# Revit family: Electrical-Box_FSR_RFL45-D2G
name_source: partatom
category: Electrical Fixtures
units: mm (PartAtom-declared; Revit-internal decimal feet)

## family parameters
Cut with Voids When Loaded = No
Host = Face
Maintain Annotation Orientation = No
Part Type = Normal
Room Calculation Point = No
Round Connector Dimension = Use Diameter
Shared = No

## types (3) — shared parameters
Apparent Load = 0 VA
Assembly Code = D5020100
Body Material = Material and Finish as Specified in 26 27 26
Building Codes = ftp://doclib.fsrinc.com/
Connections = (2) - 1/2"; (6) - 1/2 - 3/4; (2) 1" - 1 1/4" Knockouts; (3) 1x2" Oval Knockouts
Construction Details = ftp://doclib.fsrinc.com/
Default Elevation = 48 "
Green Building-LEED = http://www.arcat.com
Installation-Fabrication = ftp://doclib.fsrinc.com/
Keynote = 26 27 26
Manufacturer = FSR Inc.
Manufacturer Fax = 973-785-4207
Manufacturer Website = http://www.fsrinc.com
Model = RFL4.5-D2G
Pole = 1
Product Data = http://www.arcat.com
Sales Information = http://www.fsrinc.com
Send Message = http://admin.arcat.com
Specification = http://www.arcat.com
Test Data = ftp://doclib.fsrinc.com/
Trim Material = Material and Finish as Specified in 26 27 26
URL = http://www.fsrinc.com
Voltage = 120 V
zero-valued in all types: Expected Lifespan (Years), Maintenance Schedule (Months), Warranty Duration (Years)

## per-type parameters (varying)
| type | Cover Material | Description |
| Black Cover | Black | FSR RFL4.5-D2G - Black Cover |
| Gray Cover | Gray | FSR RFL4.5-D2G - Gray Cover |
| Tan Cover | Tan | FSR RFL4.5-D2G - Tan Cover |

## geometry (parser evidence)
native form markers: Sweep x2
no freeform markers — native parametric forms only
